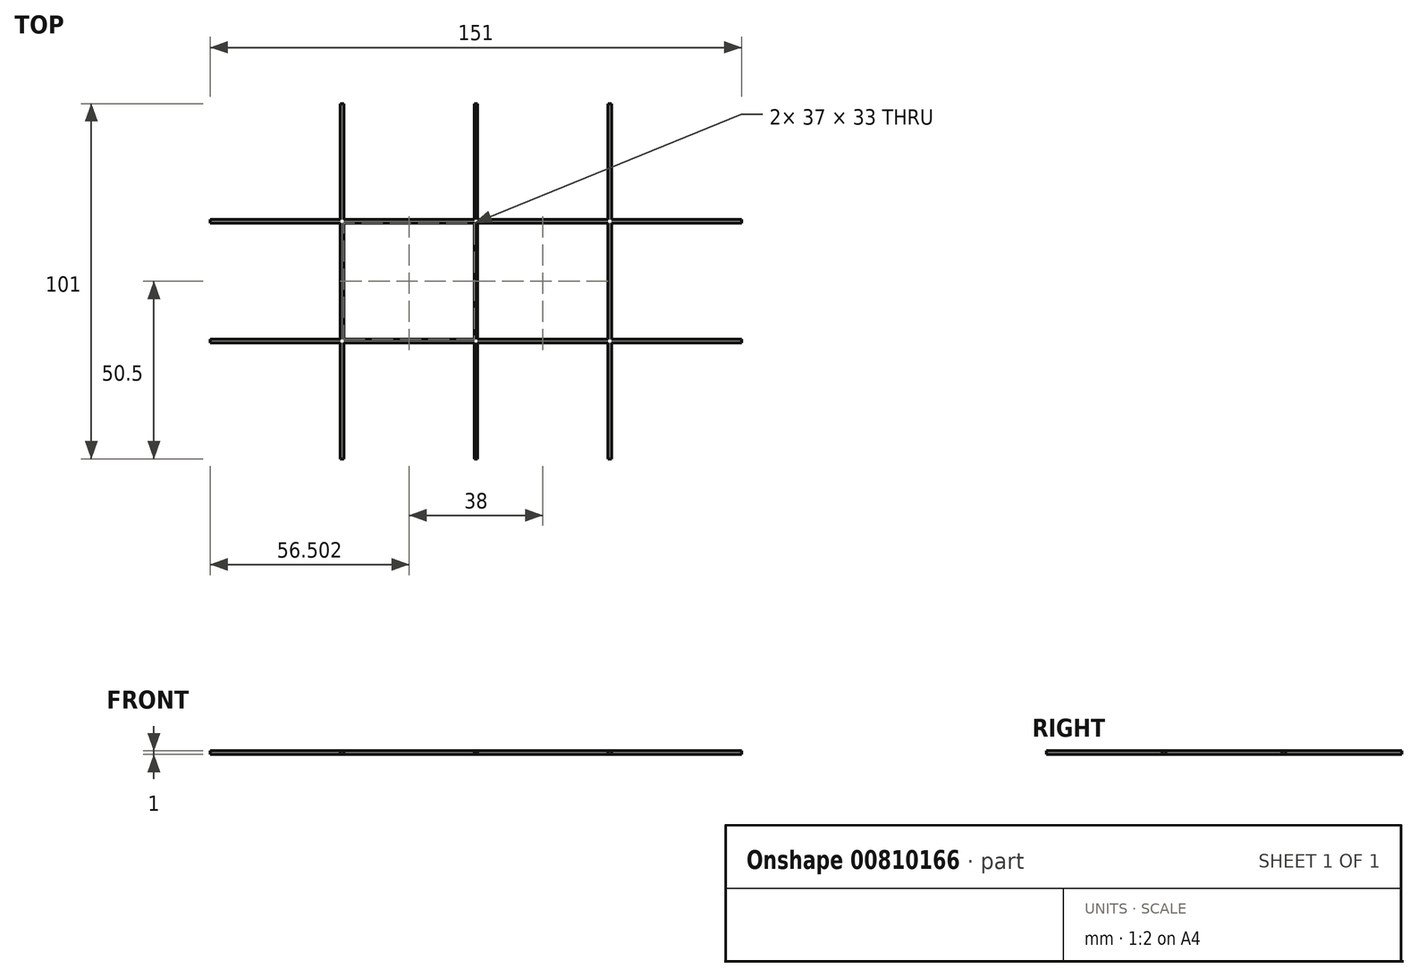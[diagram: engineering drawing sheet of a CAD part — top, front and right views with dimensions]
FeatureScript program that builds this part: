
annotation { "Feature Type Name" : "Feature", "Feature Type Description" : "" }
export const myFeature = defineFeature(function(context is Context, id is Id, definition is map)
    precondition{}
    {
        {
            var Q0;
            Q0=qCreatedBy(makeId("Top.planeOp"),FACE);
            var sketch = newSketch(context, id + "F0", { "sketchPlane" : qUnion([Q0])});
            skLineSegment(sketch, "E0.bottom", {"start": v(-73.42, 50.5) * mm, "end": v(77.58, 50.5) * mm});
            skLineSegment(sketch, "E0.top", {"start": v(-73.42, -50.5) * mm, "end": v(77.58, -50.5) * mm});
            skLineSegment(sketch, "E0.left", {"start": v(-73.42, 50.5) * mm, "end": v(-73.42, -50.5) * mm});
            skLineSegment(sketch, "E0.right", {"start": v(77.58, 50.5) * mm, "end": v(77.58, -50.5) * mm});
            skPoint(sketch, "E1", {"position": v(-73.42, 17.5) * mm});
            skPoint(sketch, "E2", {"position": v(-36.42, 17.5) * mm});
            skLineSegment(sketch, "E3", {"start": v(-73.42, 17.5) * mm, "end": v(-36.42, 17.5) * mm});
            skLineSegment(sketch, "E4", {"start": v(-36.42, 17.5) * mm, "end": v(-36.42, 50.5) * mm});
            skPoint(sketch, "E5", {"position": v(-73.42, 16.5) * mm});
            skPoint(sketch, "E6", {"position": v(-36.42, 16.5) * mm});
            skLineSegment(sketch, "E7", {"start": v(-73.42, 16.5) * mm, "end": v(-36.42, 16.5) * mm});
            skLineSegment(sketch, "E8", {"start": v(-36.42, 16.5) * mm, "end": v(-36.42, -16.5) * mm});
            skLineSegment(sketch, "E9", {"start": v(-36.42, -16.5) * mm, "end": v(-73.42, -16.5) * mm});
            skLineSegment(sketch, "E10", {"start": v(-73.42, -17.5) * mm, "end": v(-36.42, -17.5) * mm});
            skLineSegment(sketch, "E11", {"start": v(-36.42, -17.5) * mm, "end": v(-36.42, -50.5) * mm});
            skLineSegment(sketch, "E12", {"start": v(-35.42, 50.5) * mm, "end": v(-35.42, 17.5) * mm});
            skLineSegment(sketch, "E13", {"start": v(1.58, 17.5) * mm, "end": v(1.58, 50.5) * mm});
            skLineSegment(sketch, "E14", {"start": v(-35.42, 17.5) * mm, "end": v(1.58, 17.5) * mm});
            skPoint(sketch, "E15", {"position": v(-35.42, -16.5) * mm});
            skPoint(sketch, "E16", {"position": v(-35.42, 16.5) * mm});
            skLineSegment(sketch, "E17", {"start": v(-35.42, 16.5) * mm, "end": v(-35.42, -16.5) * mm});
            skPoint(sketch, "E18", {"position": v(1.58, 16.5) * mm});
            skLineSegment(sketch, "E19", {"start": v(-35.42, 16.5) * mm, "end": v(1.58, 16.5) * mm});
            skPoint(sketch, "E20", {"position": v(1.58, -16.5) * mm});
            skLineSegment(sketch, "E21", {"start": v(-35.42, -16.5) * mm, "end": v(1.58, -16.5) * mm});
            skLineSegment(sketch, "E22", {"start": v(1.58, -16.5) * mm, "end": v(1.58, 16.5) * mm});
            skPoint(sketch, "E23", {"position": v(-35.42, -17.5) * mm});
            skPoint(sketch, "E24", {"position": v(1.58, -17.5) * mm});
            skLineSegment(sketch, "E25", {"start": v(-35.42, -17.5) * mm, "end": v(1.58, -17.5) * mm});
            skLineSegment(sketch, "E26", {"start": v(-35.42, -17.5) * mm, "end": v(-35.42, -50.5) * mm});
            skLineSegment(sketch, "E27", {"start": v(1.58, -17.5) * mm, "end": v(1.58, -50.5) * mm});
            skPoint(sketch, "E28", {"position": v(2.58, -50.5) * mm});
            skPoint(sketch, "E29", {"position": v(2.58, -17.5) * mm});
            skPoint(sketch, "E30", {"position": v(2.58, -16.5) * mm});
            skPoint(sketch, "E31", {"position": v(2.58, 16.5) * mm});
            skPoint(sketch, "E32", {"position": v(2.58, 17.5) * mm});
            skPoint(sketch, "E33", {"position": v(2.58, 50.5) * mm});
            skLineSegment(sketch, "E34", {"start": v(2.58, -50.5) * mm, "end": v(2.58, -17.5) * mm});
            skLineSegment(sketch, "E35", {"start": v(2.58, -16.5) * mm, "end": v(2.58, 16.5) * mm});
            skLineSegment(sketch, "E36", {"start": v(2.58, 17.5) * mm, "end": v(2.58, 50.5) * mm});
            skPoint(sketch, "E37", {"position": v(39.58, -50.5) * mm});
            skPoint(sketch, "E38", {"position": v(39.58, -17.5) * mm});
            skPoint(sketch, "E39", {"position": v(39.58, -16.5) * mm});
            skPoint(sketch, "E40", {"position": v(39.58, 16.5) * mm});
            skPoint(sketch, "E41", {"position": v(39.58, 17.5) * mm});
            skPoint(sketch, "E42", {"position": v(39.58, 50.5) * mm});
            skLineSegment(sketch, "E43", {"start": v(2.58, 17.5) * mm, "end": v(39.58, 17.5) * mm});
            skLineSegment(sketch, "E44", {"start": v(39.58, 16.5) * mm, "end": v(2.58, 16.5) * mm});
            skLineSegment(sketch, "E45", {"start": v(39.58, -16.5) * mm, "end": v(39.58, 16.5) * mm});
            skLineSegment(sketch, "E46", {"start": v(39.58, -16.5) * mm, "end": v(2.58, -16.5) * mm});
            skLineSegment(sketch, "E47", {"start": v(2.58, -17.5) * mm, "end": v(39.58, -17.5) * mm});
            skLineSegment(sketch, "E48", {"start": v(39.58, -50.5) * mm, "end": v(39.58, -17.5) * mm});
            skLineSegment(sketch, "E49", {"start": v(39.58, 50.5) * mm, "end": v(39.58, 17.5) * mm});
            skPoint(sketch, "E50", {"position": v(40.58, -50.5) * mm});
            skPoint(sketch, "E51", {"position": v(40.58, -17.5) * mm});
            skPoint(sketch, "E52", {"position": v(40.58, -16.5) * mm});
            skPoint(sketch, "E53", {"position": v(40.58, 16.5) * mm});
            skPoint(sketch, "E54", {"position": v(40.58, 17.5) * mm});
            skPoint(sketch, "E55", {"position": v(40.58, 50.5) * mm});
            skLineSegment(sketch, "E56", {"start": v(40.58, 50.5) * mm, "end": v(40.58, 17.5) * mm});
            skLineSegment(sketch, "E57", {"start": v(40.58, 16.5) * mm, "end": v(40.58, -16.5) * mm});
            skLineSegment(sketch, "E58", {"start": v(40.58, -17.5) * mm, "end": v(40.58, -50.5) * mm});
            skLineSegment(sketch, "E59", {"start": v(40.58, -17.5) * mm, "end": v(77.58, -17.5) * mm});
            skLineSegment(sketch, "E60", {"start": v(40.58, -16.5) * mm, "end": v(77.58, -16.5) * mm});
            skLineSegment(sketch, "E61", {"start": v(40.58, 17.5) * mm, "end": v(77.58, 17.5) * mm});
            skLineSegment(sketch, "E62", {"start": v(40.58, 16.5) * mm, "end": v(77.58, 16.5) * mm});
            skLineSegment(sketch, "E63", {"start": v(-73.42, 17.5) * mm, "end": v(-73.42, 16.5) * mm});
            skLineSegment(sketch, "E64", {"start": v(-73.42, -16.5) * mm, "end": v(-73.42, -17.5) * mm});
            skLineSegment(sketch, "E65", {"start": v(-35.42, -16.5) * mm, "end": v(-35.42, -17.5) * mm});
            skSolve(sketch);
        }
        {
            var Q0;
            Q0=makeQuery(id+"F0.imprint","IMPRINT",FACE,{"disambiguationData":[TD([[makeQuery(id+"F0.imprint","IMPRINT",EDGE,{"derivedFrom":sQuery(id+"F0.wireOp",EDGE,"E3")}),-1.0]])]});
            extrude(context, id + "F1", {"entities" : qUnion([Q0]), "depth" : 1 * mm, "offsetDistance" : 25 * mm});
        }
    });
